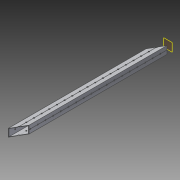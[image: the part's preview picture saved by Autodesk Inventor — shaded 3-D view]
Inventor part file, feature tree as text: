
AUTODESK INVENTOR PART (.ipt)
format: ipt  version: 2014 SP1 (Build 180222100, 222)  size: 1,311,232 bytes
history: native  units: in
note: dims shown in document units (in); Inventor stores cm internally (conversion verified against a paired STEP export)
features: extrude x3, sketch x3, pattern_circular x1, other x1, plane x1, imported_body x1
ambient origin geometry x8: Origin, YZ Plane, XZ Plane, XY Plane, X Axis, Y Axis, Z Axis, Center Point
bodies: Body1 (feature_tree)
feature tree (10):
  pattern_circular  "CirPattern2"
  other  "217-3426-STEP1"
  plane  "Work Plane1"
  extrude  "Extrusion1"  Depth=3937.0079in TaperAngle=0.0deg
  extrude  "Extrusion3"  Depth=3.937in TaperAngle=0.0deg
  extrude  "Extrusion4"  [1 undecoded]
  imported_body  "Base1"
  sketch  "Sketch1"  dims[d0=-21.0in d1=3937.0079in d2=0.0in]
  sketch  "Sketch4"  dims[d5=3.937in d6=0.0in d7=3.937in d8=0.0in]
  sketch  "Sketch5"
note: 1 required parameter value undecoded (feature->parameter linkage not recoverable at this tier; creation-order binding heuristic only, values carry confidence <= 0.55)
